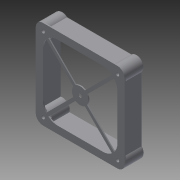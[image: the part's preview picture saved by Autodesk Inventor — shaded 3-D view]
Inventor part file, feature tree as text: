
AUTODESK INVENTOR PART (.ipt)
format: ipt  version: 2014 SP2 (Build 180246200, 246)  size: 278,016 bytes
history: native  units: mm
features: chamfer x5, extrude x2, sketch x2, fillet x1
ambient origin geometry x8: Origin, YZ Plane, XZ Plane, XY Plane, X Axis, Y Axis, Z Axis, Center Point
bodies: Solid1 (feature_tree)
feature tree (10):
  extrude  "Extrusion1"  Depth=86.0mm
  extrude  "Extrusion2"  Depth=1.5mm
  fillet  "Fillet2"  Radius=43.0mm
  chamfer  "Chamfer2"  Distance=3.5mm
  chamfer  "Chamfer3"  Distance=3.5mm
  chamfer  "Chamfer4"  Distance=3.5mm
  chamfer  "Chamfer5"  Distance=1.0mm
  chamfer  "Chamfer6"  Distance=7.0mm
  sketch  "Sketch1"  dims[d0=3.0mm d1=86.0mm]
  sketch  "Sketch3"  dims[d2=86.0mm d3=43.0mm d4=43.0mm d9=3.5mm d11=3.5mm d12=3.5mm d13=1.0mm d14=0.0mm d20=7.0mm d25=3.5mm d26=7.0mm d27=7.0mm d29=7.0mm d30=7.0mm d31=7.0mm d32=7.0mm d33=7.0mm d34=7.0mm d35=72.0mm d36=5.0mm d37=5.0mm d38=5.0mm d39=5.0mm d40=76.0mm d41=76.0mm d42=3.0mm d43=3.0mm d44=3.0mm d45=3.0mm d46=18.0mm d47=0.0mm d49=1.0mm d50=7.0mm d51=14.0mm d52=16.0mm d53=1.5mm d54=1.5mm d55=1.5mm d56=1.5mm d60=0.93mm d61=2.0mm d62=45.0deg d63=0.93mm d64=2.0mm d65=45.0deg d66=0.93mm d67=2.0mm d68=45.0deg d69=0.93mm d70=2.0mm d71=45.0deg d72=6.0mm d73=0.5mm d74=45.0deg]
